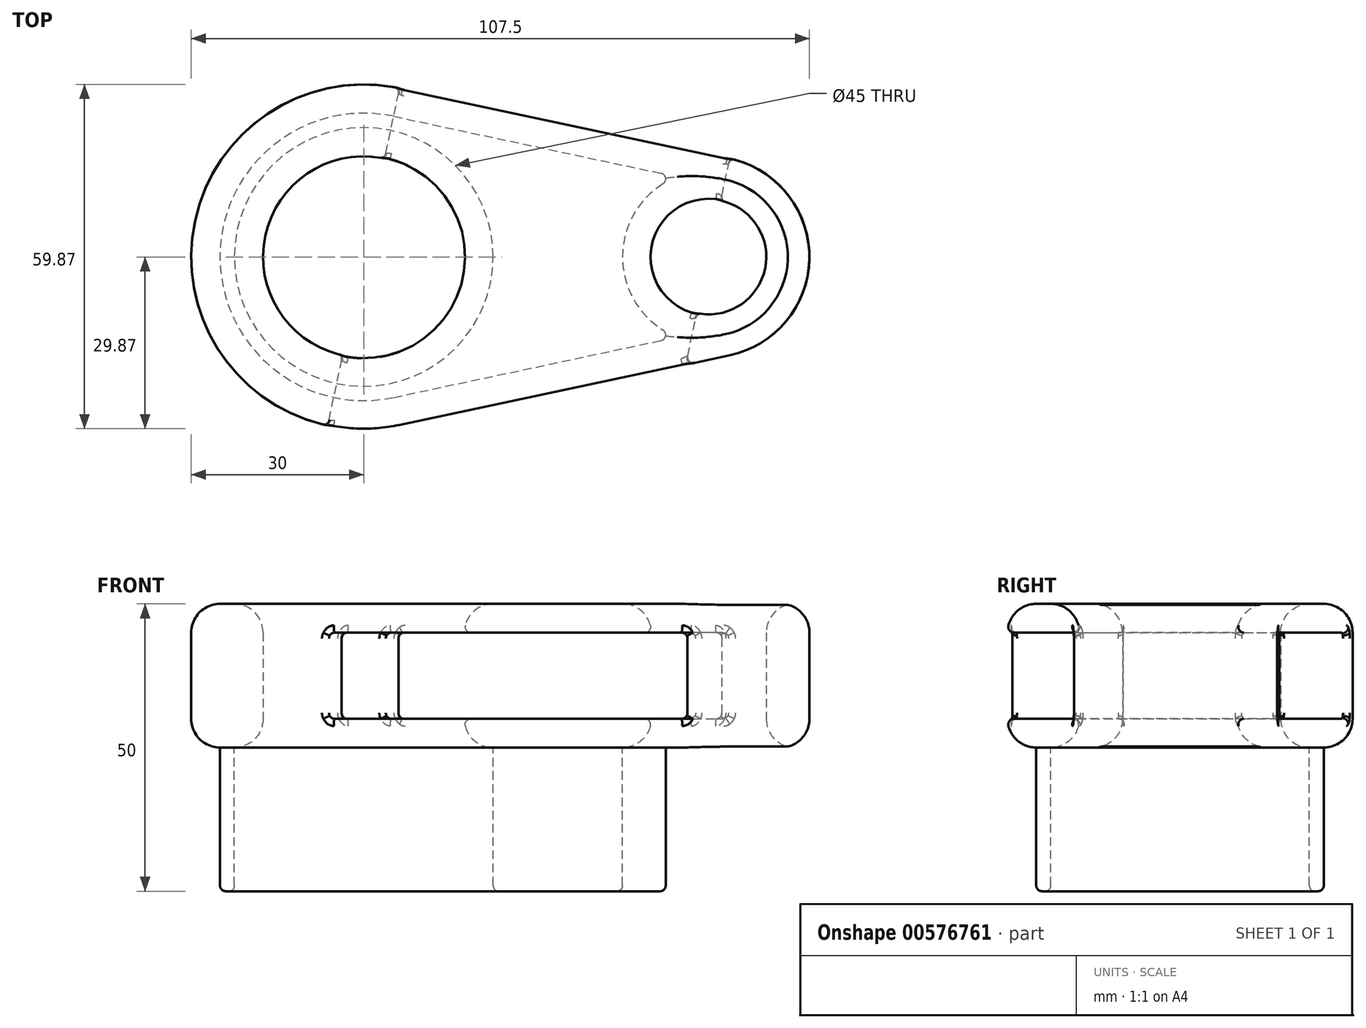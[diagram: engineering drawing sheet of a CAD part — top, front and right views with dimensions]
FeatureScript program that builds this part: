
annotation { "Feature Type Name" : "Feature", "Feature Type Description" : "" }
export const myFeature = defineFeature(function(context is Context, id is Id, definition is map)
    precondition{}
    {
        {
            var Q0;
            Q0=qCreatedBy(makeId("Top.planeOp"),FACE);
            var sketch = newSketch(context, id + "F0", { "sketchPlane" : qUnion([Q0])});
            skCircle(sketch, "E0", {"center": v(0, 0) * mm, "radius": 30 * mm});
            skCircle(sketch, "E1", {"center": v(60, 0) * mm, "radius": 17.5 * mm});
            skLineSegment(sketch, "E2", {"start": v(6.25, 29.34) * mm, "end": v(63.65, 17.12) * mm});
            skLineSegment(sketch, "E3", {"start": v(6.25, -29.34) * mm, "end": v(63.65, -17.12) * mm});
            skCircle(sketch, "E4", {"center": v(0, 0) * mm, "radius": 17.5 * mm});
            skCircle(sketch, "E5", {"center": v(60, 0) * mm, "radius": 10 * mm});
            skSolve(sketch);
        }
        {
            var Q0;
            {var subQ0=sQuery(id+"F0.wireOp",EDGE,"E2");Q0=makeQuery(id+"F0.imprint","IMPRINT",FACE,{"disambiguationData":[TD([[makeQuery(id+"F0.imprint","IMPRINT",EDGE,{"derivedFrom":subQ0}),-1.0]])]});}
            var Q1;
            Q1=makeQuery(id+"F0.imprint","IMPRINT",FACE,{"disambiguationData":[TD([[makeQuery(id+"F0.imprint","IMPRINT",EDGE,{"derivedFrom":sQuery(id+"F0.wireOp",EDGE,"E4")}),-1.0]])]});
            var Q2;
            Q2=makeQuery(id+"F0.imprint","IMPRINT",FACE,{"disambiguationData":[TD([[makeQuery(id+"F0.imprint","IMPRINT",EDGE,{"derivedFrom":sQuery(id+"F0.wireOp",EDGE,"E5")}),-1.0]])]});
            extrude(context, id + "F1", {"entities" : qUnion([Q0, Q1, Q2]), "depth" : 25 * mm, "offsetDistance" : 25 * mm});
        }
        {
            var Q0;
            Q0=makeQuery(id+"F1.opExtrude","CAP_EDGE",EDGE,{"disambiguationData":[OSD([sQuery(id+"F0.wireOp",EDGE,"E4")])],"isStart":false});
            var Q1;
            Q1=makeQuery(id+"F1.opExtrude","CAP_EDGE",EDGE,{"disambiguationData":[OSD([sQuery(id+"F0.wireOp",EDGE,"E2")])],"isStart":false});
            var Q2;
            Q2=makeQuery(id+"F1.opExtrude","CAP_EDGE",EDGE,{"disambiguationData":[OSD([sQuery(id+"F0.wireOp",EDGE,"E5")])],"isStart":false});
            var Q3;
            Q3=makeQuery(id+"F1.opExtrude","CAP_EDGE",EDGE,{"disambiguationData":[OSD([sQuery(id+"F0.wireOp",EDGE,"E4")])],"isStart":true});
            var Q4;
            Q4=makeQuery(id+"F1.opExtrude","CAP_EDGE",EDGE,{"disambiguationData":[OSD([sQuery(id+"F0.wireOp",EDGE,"E0")])],"isStart":true});
            var Q5;
            Q5=makeQuery(id+"F1.opExtrude","CAP_EDGE",EDGE,{"disambiguationData":[OSD([sQuery(id+"F0.wireOp",EDGE,"E5")])],"isStart":true});
            fillet(context, id + "F2", {"entities" : qUnion([Q0, Q1, Q2, Q3, Q4, Q5]), "radius" : 5 * mm, "tangentPropagation" : true, "allowEdgeOverflow" : false});
        }
        {
            var Q0;
            Q0=makeQuery(id+"F1.opExtrude","SWEPT_FACE",FACE,{"disambiguationData":[OSD([sQuery(id+"F0.wireOp",EDGE,"E2")])]});
            extrude(context, id + "F3", {"entities" : qUnion([Q0]), "operationType" : NewBodyOperationType.REMOVE, "endBound" : BoundingType.THROUGH_ALL, "oppositeDirection" : true, "depth" : 25 * mm, "offsetDistance" : 25 * mm});
        }
        {
            var Q0;
            {var subQ0=sQuery(id+"F0.wireOp",EDGE,"E2");var subQ1=sQuery(id+"F0.wireOp",EDGE,"E1");Q0=makeQuery(id+"F3.boolean.opBoolean","MERGE",EDGE,{"derivedFrom":[makeQuery(id+"F1.opExtrude","SWEPT_EDGE",EDGE,{"disambiguationData":[OSD([subQ1,subQ0])]}),makeQuery(id+"F3.opExtrude","CAP_EDGE",EDGE,{"disambiguationData":[OSD([subQ1,subQ0])],"isStart":true})]});}
            var Q1;
            {var subQ0=sQuery(id+"F0.wireOp",EDGE,"E2");var subQ1=makeQuery(id+"F2.opFillet","BLEND_EDGE",EDGE,{"blendedFrom":[makeQuery(id+"F1.opExtrude","CAP_EDGE",EDGE,{"disambiguationData":[OSD([subQ0])],"isStart":true}),makeQuery(id+"F1.opExtrude","SWEPT_FACE",FACE,{"disambiguationData":[OSD([subQ0])]})],"blendedInto":[makeQuery(id+"F1.opExtrude","SWEPT_FACE",FACE,{"disambiguationData":[OSD([subQ0])]})]});Q1=makeQuery(id+"F3.boolean.opBoolean","MERGE",EDGE,{"derivedFrom":[subQ1,makeQuery(id+"F3.opExtrude","CAP_EDGE",EDGE,{"disambiguationData":[OSD([subQ0]),TDD([subQ1])],"isStart":true})]});}
            var Q2;
            {var subQ0=sQuery(id+"F0.wireOp",EDGE,"E2");var subQ1=sQuery(id+"F0.wireOp",EDGE,"E0");Q2=makeQuery(id+"F3.boolean.opBoolean","MERGE",EDGE,{"derivedFrom":[makeQuery(id+"F1.opExtrude","SWEPT_EDGE",EDGE,{"disambiguationData":[OSD([subQ1,subQ0])]}),makeQuery(id+"F3.opExtrude","CAP_EDGE",EDGE,{"disambiguationData":[OSD([subQ1,subQ0])],"isStart":true})]});}
            var Q3;
            {var subQ0=sQuery(id+"F0.wireOp",EDGE,"E2");var subQ1=makeQuery(id+"F2.opFillet","BLEND_EDGE",EDGE,{"blendedFrom":[makeQuery(id+"F1.opExtrude","CAP_EDGE",EDGE,{"disambiguationData":[OSD([subQ0])],"isStart":false}),makeQuery(id+"F1.opExtrude","SWEPT_FACE",FACE,{"disambiguationData":[OSD([subQ0])]})],"blendedInto":[makeQuery(id+"F1.opExtrude","SWEPT_FACE",FACE,{"disambiguationData":[OSD([subQ0])]})]});Q3=makeQuery(id+"F3.boolean.opBoolean","MERGE",EDGE,{"derivedFrom":[subQ1,makeQuery(id+"F3.opExtrude","CAP_EDGE",EDGE,{"disambiguationData":[OSD([subQ0]),TDD([subQ1])],"isStart":true})]});}
            var Q4;
            {var subQ0=sQuery(id+"F0.wireOp",EDGE,"E0");var subQ1=makeQuery(id+"F1.opExtrude","CAP_EDGE",EDGE,{"disambiguationData":[OSD([subQ0])],"isStart":true});var subQ2=sQuery(id+"F0.wireOp",EDGE,"E4");var subQ3=sQuery(id+"F0.wireOp",EDGE,"E2");var subQ4=makeQuery(id+"F1.opExtrude","CAP_EDGE",EDGE,{"disambiguationData":[OSD([subQ3])],"isStart":true});var subQ5=makeQuery(id+"F1.opExtrude","SWEPT_FACE",FACE,{"disambiguationData":[OSD([subQ0])]});var subQ6=makeQuery(id+"F1.opExtrude","SWEPT_FACE",FACE,{"disambiguationData":[OSD([subQ3])]});Q4=makeQuery(id+"F3.boolean.opBoolean","COPY",EDGE,{"disambiguationData":[TD([subQ5,makeQuery(id+"F1.opExtrude","SWEPT_FACE",FACE,{"disambiguationData":[OSD([subQ2])]}),makeQuery(id+"F2.opFillet","BLEND_FACE",FACE,{"disambiguationData":[OSD([subQ0]),TDD([subQ1])]}),makeQuery(id+"F2.opFillet","BLEND_FACE",FACE,{"disambiguationData":[OSD([subQ3]),TDD([subQ4])]}),makeQuery(id+"F2.opFillet","BLEND_FACE",FACE,{"disambiguationData":[OSD([subQ2]),TDD([makeQuery(id+"F1.opExtrude","CAP_EDGE",EDGE,{"disambiguationData":[OSD([subQ2])],"isStart":true})])]}),makeQuery(id+"F3.opExtrude","SWEPT_FACE",FACE,{"disambiguationData":[OSD([subQ0,subQ3])]}),makeQuery(id+"F3.opExtrude","SWEPT_FACE",FACE,{"disambiguationData":[OSD([subQ3]),TDD([makeQuery(id+"F2.opFillet","BLEND_EDGE",EDGE,{"blendedFrom":[subQ4,subQ6],"blendedInto":[subQ6]})])]})])],"derivedFrom":makeQuery(id+"F3.opExtrude","SWEPT_EDGE",EDGE,{"disambiguationData":[OSD([subQ0,subQ3]),TDD([makeQuery(id+"F2.opFillet","BLEND_VERTEX",VERTEX,{"blendedFrom":[subQ1,subQ4,subQ5,subQ6],"blendedInto":[subQ5,subQ6]})])]})});}
            var Q5;
            {var subQ0=sQuery(id+"F0.wireOp",EDGE,"E0");var subQ1=makeQuery(id+"F1.opExtrude","CAP_EDGE",EDGE,{"disambiguationData":[OSD([subQ0])],"isStart":false});var subQ2=sQuery(id+"F0.wireOp",EDGE,"E2");var subQ3=makeQuery(id+"F1.opExtrude","CAP_EDGE",EDGE,{"disambiguationData":[OSD([subQ2])],"isStart":false});var subQ4=sQuery(id+"F0.wireOp",EDGE,"E4");var subQ5=makeQuery(id+"F1.opExtrude","SWEPT_FACE",FACE,{"disambiguationData":[OSD([subQ0])]});var subQ6=makeQuery(id+"F1.opExtrude","SWEPT_FACE",FACE,{"disambiguationData":[OSD([subQ2])]});Q5=makeQuery(id+"F3.boolean.opBoolean","COPY",EDGE,{"disambiguationData":[TD([subQ5,makeQuery(id+"F1.opExtrude","SWEPT_FACE",FACE,{"disambiguationData":[OSD([subQ4])]}),makeQuery(id+"F2.opFillet","BLEND_FACE",FACE,{"disambiguationData":[OSD([subQ0]),TDD([subQ1])]}),makeQuery(id+"F2.opFillet","BLEND_FACE",FACE,{"disambiguationData":[OSD([subQ2]),TDD([subQ3])]}),makeQuery(id+"F2.opFillet","BLEND_FACE",FACE,{"disambiguationData":[OSD([subQ4]),TDD([makeQuery(id+"F1.opExtrude","CAP_EDGE",EDGE,{"disambiguationData":[OSD([subQ4])],"isStart":false})])]}),makeQuery(id+"F3.opExtrude","SWEPT_FACE",FACE,{"disambiguationData":[OSD([subQ0,subQ2])]}),makeQuery(id+"F3.opExtrude","SWEPT_FACE",FACE,{"disambiguationData":[OSD([subQ2]),TDD([makeQuery(id+"F2.opFillet","BLEND_EDGE",EDGE,{"blendedFrom":[subQ3,subQ6],"blendedInto":[subQ6]})])]})])],"derivedFrom":makeQuery(id+"F3.opExtrude","SWEPT_EDGE",EDGE,{"disambiguationData":[OSD([subQ0,subQ2]),TDD([makeQuery(id+"F2.opFillet","BLEND_VERTEX",VERTEX,{"blendedFrom":[subQ1,subQ3,subQ5,subQ6],"blendedInto":[subQ5,subQ6]})])]})});}
            var Q6;
            {var subQ0=sQuery(id+"F0.wireOp",EDGE,"E2");var subQ1=makeQuery(id+"F1.opExtrude","CAP_EDGE",EDGE,{"disambiguationData":[OSD([subQ0])],"isStart":false});var subQ2=sQuery(id+"F0.wireOp",EDGE,"E1");var subQ3=makeQuery(id+"F1.opExtrude","CAP_EDGE",EDGE,{"disambiguationData":[OSD([subQ2])],"isStart":false});var subQ5=makeQuery(id+"F1.opExtrude","SWEPT_FACE",FACE,{"disambiguationData":[OSD([subQ2])]});var subQ6=makeQuery(id+"F1.opExtrude","SWEPT_FACE",FACE,{"disambiguationData":[OSD([subQ0])]});Q6=makeQuery(id+"F3.boolean.opBoolean","COPY",EDGE,{"disambiguationData":[TD([subQ5])],"derivedFrom":makeQuery(id+"F3.opExtrude","SWEPT_EDGE",EDGE,{"disambiguationData":[OSD([subQ2,subQ0]),TDD([makeQuery(id+"F2.opFillet","BLEND_VERTEX",VERTEX,{"blendedFrom":[subQ3,subQ1,subQ5,subQ6],"blendedInto":[subQ5,subQ6]})])]})});}
            var Q7;
            {var subQ0=sQuery(id+"F0.wireOp",EDGE,"E2");var subQ1=makeQuery(id+"F1.opExtrude","CAP_EDGE",EDGE,{"disambiguationData":[OSD([subQ0])],"isStart":true});var subQ3=sQuery(id+"F0.wireOp",EDGE,"E1");var subQ4=makeQuery(id+"F1.opExtrude","CAP_EDGE",EDGE,{"disambiguationData":[OSD([subQ3])],"isStart":true});var subQ5=makeQuery(id+"F1.opExtrude","SWEPT_FACE",FACE,{"disambiguationData":[OSD([subQ3])]});var subQ6=makeQuery(id+"F1.opExtrude","SWEPT_FACE",FACE,{"disambiguationData":[OSD([subQ0])]});Q7=makeQuery(id+"F3.boolean.opBoolean","COPY",EDGE,{"disambiguationData":[TD([subQ5])],"derivedFrom":makeQuery(id+"F3.opExtrude","SWEPT_EDGE",EDGE,{"disambiguationData":[OSD([subQ3,subQ0]),TDD([makeQuery(id+"F2.opFillet","BLEND_VERTEX",VERTEX,{"blendedFrom":[subQ4,subQ1,subQ5,subQ6],"blendedInto":[subQ5,subQ6]})])]})});}
            var Q8;
            {var subQ0=sQuery(id+"F0.wireOp",EDGE,"E5");var subQ1=makeQuery(id+"F1.opExtrude","CAP_EDGE",EDGE,{"disambiguationData":[OSD([subQ0])],"isStart":false});var subQ2=sQuery(id+"F0.wireOp",EDGE,"E2");Q8=makeQuery(id+"F3.boolean.opBoolean","SPLIT",EDGE,{"disambiguationData":[topologyDisambiguationEdgeConnected([makeQuery(id+"F3.opExtrude","SWEPT_FACE",FACE,{"disambiguationData":[OSD([subQ2]),TDD([makeQuery(id+"F2.opFillet","BLEND_EDGE",EDGE,{"blendedFrom":[makeQuery(id+"F1.opExtrude","CAP_EDGE",EDGE,{"disambiguationData":[OSD([subQ2])],"isStart":false}),makeQuery(id+"F1.opExtrude","SWEPT_FACE",FACE,{"disambiguationData":[OSD([subQ2])]})],"blendedInto":[makeQuery(id+"F1.opExtrude","SWEPT_FACE",FACE,{"disambiguationData":[OSD([subQ2])]})]})])]})])],"derivedFrom":makeQuery(id+"F2.opFillet","BLEND_EDGE",EDGE,{"blendedFrom":[subQ1,makeQuery(id+"F1.opExtrude","SWEPT_FACE",FACE,{"disambiguationData":[OSD([subQ0])]})],"blendedInto":[makeQuery(id+"F1.opExtrude","SWEPT_FACE",FACE,{"disambiguationData":[OSD([subQ0])]})]})});}
            var Q9;
            Q9=makeQuery(id+"F3.boolean.opBoolean","INTERSECT",EDGE,{"disambiguationData":[OD(0.0)],"derivedFrom":[makeQuery(id+"F1.opExtrude","SWEPT_FACE",FACE,{"disambiguationData":[OSD([sQuery(id+"F0.wireOp",EDGE,"E5")])]}),makeQuery(id+"F3.opExtrude","SWEPT_FACE",FACE,{"disambiguationData":[OSD([sQuery(id+"F0.wireOp",EDGE,"E1"),sQuery(id+"F0.wireOp",EDGE,"E2")])]})]});
            var Q10;
            {var subQ0=sQuery(id+"F0.wireOp",EDGE,"E5");var subQ1=makeQuery(id+"F1.opExtrude","CAP_EDGE",EDGE,{"disambiguationData":[OSD([subQ0])],"isStart":true});var subQ2=sQuery(id+"F0.wireOp",EDGE,"E2");Q10=makeQuery(id+"F3.boolean.opBoolean","SPLIT",EDGE,{"disambiguationData":[topologyDisambiguationEdgeConnected([makeQuery(id+"F3.opExtrude","SWEPT_FACE",FACE,{"disambiguationData":[OSD([subQ2]),TDD([makeQuery(id+"F2.opFillet","BLEND_EDGE",EDGE,{"blendedFrom":[makeQuery(id+"F1.opExtrude","CAP_EDGE",EDGE,{"disambiguationData":[OSD([subQ2])],"isStart":true}),makeQuery(id+"F1.opExtrude","SWEPT_FACE",FACE,{"disambiguationData":[OSD([subQ2])]})],"blendedInto":[makeQuery(id+"F1.opExtrude","SWEPT_FACE",FACE,{"disambiguationData":[OSD([subQ2])]})]})])]})])],"derivedFrom":makeQuery(id+"F2.opFillet","BLEND_EDGE",EDGE,{"blendedFrom":[subQ1,makeQuery(id+"F1.opExtrude","SWEPT_FACE",FACE,{"disambiguationData":[OSD([subQ0])]})],"blendedInto":[makeQuery(id+"F1.opExtrude","SWEPT_FACE",FACE,{"disambiguationData":[OSD([subQ0])]})]})});}
            var Q11;
            Q11=makeQuery(id+"F3.boolean.opBoolean","INTERSECT",EDGE,{"disambiguationData":[OD(1.0)],"derivedFrom":[makeQuery(id+"F1.opExtrude","SWEPT_FACE",FACE,{"disambiguationData":[OSD([sQuery(id+"F0.wireOp",EDGE,"E5")])]}),makeQuery(id+"F3.opExtrude","SWEPT_FACE",FACE,{"disambiguationData":[OSD([sQuery(id+"F0.wireOp",EDGE,"E1"),sQuery(id+"F0.wireOp",EDGE,"E2")])]})]});
            var Q12;
            Q12=makeQuery(id+"F3.boolean.opBoolean","INTERSECT",EDGE,{"disambiguationData":[OD(0.0)],"derivedFrom":[makeQuery(id+"F1.opExtrude","SWEPT_FACE",FACE,{"disambiguationData":[OSD([sQuery(id+"F0.wireOp",EDGE,"E4")])]}),makeQuery(id+"F3.opExtrude","SWEPT_FACE",FACE,{"disambiguationData":[OSD([sQuery(id+"F0.wireOp",EDGE,"E0"),sQuery(id+"F0.wireOp",EDGE,"E2")])]})]});
            var Q13;
            {var subQ0=sQuery(id+"F0.wireOp",EDGE,"E4");var subQ1=makeQuery(id+"F1.opExtrude","CAP_EDGE",EDGE,{"disambiguationData":[OSD([subQ0])],"isStart":true});var subQ2=sQuery(id+"F0.wireOp",EDGE,"E2");Q13=makeQuery(id+"F3.boolean.opBoolean","SPLIT",EDGE,{"disambiguationData":[topologyDisambiguationEdgeConnected([makeQuery(id+"F3.opExtrude","SWEPT_FACE",FACE,{"disambiguationData":[OSD([subQ2]),TDD([makeQuery(id+"F2.opFillet","BLEND_EDGE",EDGE,{"blendedFrom":[makeQuery(id+"F1.opExtrude","CAP_EDGE",EDGE,{"disambiguationData":[OSD([subQ2])],"isStart":true}),makeQuery(id+"F1.opExtrude","SWEPT_FACE",FACE,{"disambiguationData":[OSD([subQ2])]})],"blendedInto":[makeQuery(id+"F1.opExtrude","SWEPT_FACE",FACE,{"disambiguationData":[OSD([subQ2])]})]})])]})])],"derivedFrom":makeQuery(id+"F2.opFillet","BLEND_EDGE",EDGE,{"blendedFrom":[subQ1,makeQuery(id+"F1.opExtrude","SWEPT_FACE",FACE,{"disambiguationData":[OSD([subQ0])]})],"blendedInto":[makeQuery(id+"F1.opExtrude","SWEPT_FACE",FACE,{"disambiguationData":[OSD([subQ0])]})]})});}
            var Q14;
            Q14=makeQuery(id+"F3.boolean.opBoolean","INTERSECT",EDGE,{"disambiguationData":[OD(1.0)],"derivedFrom":[makeQuery(id+"F1.opExtrude","SWEPT_FACE",FACE,{"disambiguationData":[OSD([sQuery(id+"F0.wireOp",EDGE,"E4")])]}),makeQuery(id+"F3.opExtrude","SWEPT_FACE",FACE,{"disambiguationData":[OSD([sQuery(id+"F0.wireOp",EDGE,"E0"),sQuery(id+"F0.wireOp",EDGE,"E2")])]})]});
            var Q15;
            {var subQ0=sQuery(id+"F0.wireOp",EDGE,"E4");var subQ1=makeQuery(id+"F1.opExtrude","CAP_EDGE",EDGE,{"disambiguationData":[OSD([subQ0])],"isStart":false});var subQ2=sQuery(id+"F0.wireOp",EDGE,"E2");Q15=makeQuery(id+"F3.boolean.opBoolean","SPLIT",EDGE,{"disambiguationData":[topologyDisambiguationEdgeConnected([makeQuery(id+"F3.opExtrude","SWEPT_FACE",FACE,{"disambiguationData":[OSD([subQ2]),TDD([makeQuery(id+"F2.opFillet","BLEND_EDGE",EDGE,{"blendedFrom":[makeQuery(id+"F1.opExtrude","CAP_EDGE",EDGE,{"disambiguationData":[OSD([subQ2])],"isStart":false}),makeQuery(id+"F1.opExtrude","SWEPT_FACE",FACE,{"disambiguationData":[OSD([subQ2])]})],"blendedInto":[makeQuery(id+"F1.opExtrude","SWEPT_FACE",FACE,{"disambiguationData":[OSD([subQ2])]})]})])]})])],"derivedFrom":makeQuery(id+"F2.opFillet","BLEND_EDGE",EDGE,{"blendedFrom":[subQ1,makeQuery(id+"F1.opExtrude","SWEPT_FACE",FACE,{"disambiguationData":[OSD([subQ0])]})],"blendedInto":[makeQuery(id+"F1.opExtrude","SWEPT_FACE",FACE,{"disambiguationData":[OSD([subQ0])]})]})});}
            var Q16;
            {var subQ0=sQuery(id+"F0.wireOp",EDGE,"E3");var subQ1=makeQuery(id+"F1.opExtrude","CAP_EDGE",EDGE,{"disambiguationData":[OSD([subQ0])],"isStart":false});var subQ2=sQuery(id+"F0.wireOp",EDGE,"E2");Q16=makeQuery(id+"F3.boolean.opBoolean","SPLIT",EDGE,{"disambiguationData":[topologyDisambiguationEdgeConnected([makeQuery(id+"F3.opExtrude","SWEPT_FACE",FACE,{"disambiguationData":[OSD([subQ2]),TDD([makeQuery(id+"F2.opFillet","BLEND_EDGE",EDGE,{"blendedFrom":[makeQuery(id+"F1.opExtrude","CAP_EDGE",EDGE,{"disambiguationData":[OSD([subQ2])],"isStart":false}),makeQuery(id+"F1.opExtrude","SWEPT_FACE",FACE,{"disambiguationData":[OSD([subQ2])]})],"blendedInto":[makeQuery(id+"F1.opExtrude","SWEPT_FACE",FACE,{"disambiguationData":[OSD([subQ2])]})]})])]})])],"derivedFrom":makeQuery(id+"F2.opFillet","BLEND_EDGE",EDGE,{"blendedFrom":[subQ1,makeQuery(id+"F1.opExtrude","SWEPT_FACE",FACE,{"disambiguationData":[OSD([subQ0])]})],"blendedInto":[makeQuery(id+"F1.opExtrude","SWEPT_FACE",FACE,{"disambiguationData":[OSD([subQ0])]})]})});}
            var Q17;
            {var subQ0=sQuery(id+"F0.wireOp",EDGE,"E0");var subQ1=makeQuery(id+"F1.opExtrude","CAP_EDGE",EDGE,{"disambiguationData":[OSD([subQ0])],"isStart":false});var subQ2=sQuery(id+"F0.wireOp",EDGE,"E2");Q17=makeQuery(id+"F3.boolean.opBoolean","SPLIT",EDGE,{"disambiguationData":[topologyDisambiguationEdgeConnected([makeQuery(id+"F3.opExtrude","SWEPT_FACE",FACE,{"disambiguationData":[OSD([subQ2]),TDD([makeQuery(id+"F2.opFillet","BLEND_EDGE",EDGE,{"blendedFrom":[makeQuery(id+"F1.opExtrude","CAP_EDGE",EDGE,{"disambiguationData":[OSD([subQ2])],"isStart":false}),makeQuery(id+"F1.opExtrude","SWEPT_FACE",FACE,{"disambiguationData":[OSD([subQ2])]})],"blendedInto":[makeQuery(id+"F1.opExtrude","SWEPT_FACE",FACE,{"disambiguationData":[OSD([subQ2])]})]})])]})])],"derivedFrom":makeQuery(id+"F2.opFillet","BLEND_EDGE",EDGE,{"blendedFrom":[subQ1,makeQuery(id+"F1.opExtrude","SWEPT_FACE",FACE,{"disambiguationData":[OSD([subQ0])]})],"blendedInto":[makeQuery(id+"F1.opExtrude","SWEPT_FACE",FACE,{"disambiguationData":[OSD([subQ0])]})]})});}
            var Q18;
            {var subQ0=sQuery(id+"F0.wireOp",EDGE,"E0");Q18=makeQuery(id+"F3.boolean.opBoolean","INTERSECT",EDGE,{"derivedFrom":[makeQuery(id+"F1.opExtrude","SWEPT_FACE",FACE,{"disambiguationData":[OSD([subQ0])]}),makeQuery(id+"F3.opExtrude","SWEPT_FACE",FACE,{"disambiguationData":[OSD([subQ0,sQuery(id+"F0.wireOp",EDGE,"E2")])]})]});}
            var Q19;
            {var subQ0=sQuery(id+"F0.wireOp",EDGE,"E0");var subQ1=makeQuery(id+"F1.opExtrude","CAP_EDGE",EDGE,{"disambiguationData":[OSD([subQ0])],"isStart":false});var subQ2=sQuery(id+"F0.wireOp",EDGE,"E4");var subQ3=makeQuery(id+"F1.opExtrude","SWEPT_FACE",FACE,{"disambiguationData":[OSD([subQ0])]});var subQ4=sQuery(id+"F0.wireOp",EDGE,"E2");var subQ5=makeQuery(id+"F1.opExtrude","SWEPT_FACE",FACE,{"disambiguationData":[OSD([subQ4])]});var subQ6=makeQuery(id+"F1.opExtrude","CAP_EDGE",EDGE,{"disambiguationData":[OSD([subQ4])],"isStart":false});Q19=makeQuery(id+"F3.boolean.opBoolean","COPY",EDGE,{"disambiguationData":[TD([subQ3,makeQuery(id+"F1.opExtrude","SWEPT_FACE",FACE,{"disambiguationData":[OSD([subQ2])]}),makeQuery(id+"F2.opFillet","BLEND_FACE",FACE,{"disambiguationData":[OSD([subQ0]),TDD([subQ1])]}),makeQuery(id+"F2.opFillet","BLEND_FACE",FACE,{"disambiguationData":[OSD([subQ2]),TDD([makeQuery(id+"F1.opExtrude","CAP_EDGE",EDGE,{"disambiguationData":[OSD([subQ2])],"isStart":false})])]}),makeQuery(id+"F3.opExtrude","SWEPT_FACE",FACE,{"disambiguationData":[OSD([subQ0,subQ4])]}),makeQuery(id+"F3.opExtrude","SWEPT_FACE",FACE,{"disambiguationData":[OSD([subQ4]),TDD([makeQuery(id+"F2.opFillet","BLEND_EDGE",EDGE,{"blendedFrom":[subQ6,subQ5],"blendedInto":[subQ5]})])]})])],"derivedFrom":makeQuery(id+"F3.opExtrude","SWEPT_EDGE",EDGE,{"disambiguationData":[OSD([subQ0,subQ4]),TDD([makeQuery(id+"F2.opFillet","BLEND_VERTEX",VERTEX,{"blendedFrom":[subQ1,subQ6,subQ3,subQ5],"blendedInto":[subQ3,subQ5]})])]})});}
            var Q20;
            {var subQ0=sQuery(id+"F0.wireOp",EDGE,"E0");var subQ1=makeQuery(id+"F1.opExtrude","CAP_EDGE",EDGE,{"disambiguationData":[OSD([subQ0])],"isStart":true});var subQ2=sQuery(id+"F0.wireOp",EDGE,"E2");Q20=makeQuery(id+"F3.boolean.opBoolean","SPLIT",EDGE,{"disambiguationData":[topologyDisambiguationEdgeConnected([makeQuery(id+"F3.opExtrude","SWEPT_FACE",FACE,{"disambiguationData":[OSD([subQ2]),TDD([makeQuery(id+"F2.opFillet","BLEND_EDGE",EDGE,{"blendedFrom":[makeQuery(id+"F1.opExtrude","CAP_EDGE",EDGE,{"disambiguationData":[OSD([subQ2])],"isStart":true}),makeQuery(id+"F1.opExtrude","SWEPT_FACE",FACE,{"disambiguationData":[OSD([subQ2])]})],"blendedInto":[makeQuery(id+"F1.opExtrude","SWEPT_FACE",FACE,{"disambiguationData":[OSD([subQ2])]})]})])]})])],"derivedFrom":makeQuery(id+"F2.opFillet","BLEND_EDGE",EDGE,{"blendedFrom":[subQ1,makeQuery(id+"F1.opExtrude","SWEPT_FACE",FACE,{"disambiguationData":[OSD([subQ0])]})],"blendedInto":[makeQuery(id+"F1.opExtrude","SWEPT_FACE",FACE,{"disambiguationData":[OSD([subQ0])]})]})});}
            var Q21;
            {var subQ0=sQuery(id+"F0.wireOp",EDGE,"E3");var subQ1=makeQuery(id+"F1.opExtrude","CAP_EDGE",EDGE,{"disambiguationData":[OSD([subQ0])],"isStart":true});var subQ2=sQuery(id+"F0.wireOp",EDGE,"E2");Q21=makeQuery(id+"F3.boolean.opBoolean","SPLIT",EDGE,{"disambiguationData":[topologyDisambiguationEdgeConnected([makeQuery(id+"F3.opExtrude","SWEPT_FACE",FACE,{"disambiguationData":[OSD([subQ2]),TDD([makeQuery(id+"F2.opFillet","BLEND_EDGE",EDGE,{"blendedFrom":[makeQuery(id+"F1.opExtrude","CAP_EDGE",EDGE,{"disambiguationData":[OSD([subQ2])],"isStart":true}),makeQuery(id+"F1.opExtrude","SWEPT_FACE",FACE,{"disambiguationData":[OSD([subQ2])]})],"blendedInto":[makeQuery(id+"F1.opExtrude","SWEPT_FACE",FACE,{"disambiguationData":[OSD([subQ2])]})]})])]})])],"derivedFrom":makeQuery(id+"F2.opFillet","BLEND_EDGE",EDGE,{"blendedFrom":[subQ1,makeQuery(id+"F1.opExtrude","SWEPT_FACE",FACE,{"disambiguationData":[OSD([subQ0])]})],"blendedInto":[makeQuery(id+"F1.opExtrude","SWEPT_FACE",FACE,{"disambiguationData":[OSD([subQ0])]})]})});}
            var Q22;
            Q22=makeQuery(id+"F3.boolean.opBoolean","INTERSECT",EDGE,{"derivedFrom":[makeQuery(id+"F1.opExtrude","SWEPT_FACE",FACE,{"disambiguationData":[OSD([sQuery(id+"F0.wireOp",EDGE,"E3")])]}),makeQuery(id+"F3.opExtrude","SWEPT_FACE",FACE,{"disambiguationData":[OSD([sQuery(id+"F0.wireOp",EDGE,"E1"),sQuery(id+"F0.wireOp",EDGE,"E2")])]})]});
            var Q23;
            {var subQ0=sQuery(id+"F0.wireOp",EDGE,"E4");var subQ1=sQuery(id+"F0.wireOp",EDGE,"E0");var subQ2=makeQuery(id+"F1.opExtrude","CAP_EDGE",EDGE,{"disambiguationData":[OSD([subQ1])],"isStart":true});var subQ3=makeQuery(id+"F1.opExtrude","SWEPT_FACE",FACE,{"disambiguationData":[OSD([subQ1])]});var subQ4=sQuery(id+"F0.wireOp",EDGE,"E2");var subQ5=makeQuery(id+"F1.opExtrude","SWEPT_FACE",FACE,{"disambiguationData":[OSD([subQ4])]});var subQ6=makeQuery(id+"F1.opExtrude","CAP_EDGE",EDGE,{"disambiguationData":[OSD([subQ4])],"isStart":true});Q23=makeQuery(id+"F3.boolean.opBoolean","COPY",EDGE,{"disambiguationData":[TD([subQ3,makeQuery(id+"F1.opExtrude","SWEPT_FACE",FACE,{"disambiguationData":[OSD([subQ0])]}),makeQuery(id+"F2.opFillet","BLEND_FACE",FACE,{"disambiguationData":[OSD([subQ1]),TDD([subQ2])]}),makeQuery(id+"F2.opFillet","BLEND_FACE",FACE,{"disambiguationData":[OSD([subQ0]),TDD([makeQuery(id+"F1.opExtrude","CAP_EDGE",EDGE,{"disambiguationData":[OSD([subQ0])],"isStart":true})])]}),makeQuery(id+"F3.opExtrude","SWEPT_FACE",FACE,{"disambiguationData":[OSD([subQ1,subQ4])]}),makeQuery(id+"F3.opExtrude","SWEPT_FACE",FACE,{"disambiguationData":[OSD([subQ4]),TDD([makeQuery(id+"F2.opFillet","BLEND_EDGE",EDGE,{"blendedFrom":[subQ6,subQ5],"blendedInto":[subQ5]})])]})])],"derivedFrom":makeQuery(id+"F3.opExtrude","SWEPT_EDGE",EDGE,{"disambiguationData":[OSD([subQ1,subQ4]),TDD([makeQuery(id+"F2.opFillet","BLEND_VERTEX",VERTEX,{"blendedFrom":[subQ2,subQ6,subQ3,subQ5],"blendedInto":[subQ3,subQ5]})])]})});}
            var Q24;
            {var subQ0=sQuery(id+"F0.wireOp",EDGE,"E3");var subQ1=sQuery(id+"F0.wireOp",EDGE,"E2");var subQ2=makeQuery(id+"F1.opExtrude","SWEPT_FACE",FACE,{"disambiguationData":[OSD([subQ1])]});var subQ3=makeQuery(id+"F1.opExtrude","CAP_EDGE",EDGE,{"disambiguationData":[OSD([subQ1])],"isStart":false});var subQ5=sQuery(id+"F0.wireOp",EDGE,"E1");Q24=makeQuery(id+"F3.boolean.opBoolean","COPY",EDGE,{"disambiguationData":[TD([makeQuery(id+"F1.opExtrude","SWEPT_FACE",FACE,{"disambiguationData":[OSD([subQ0])]})])],"derivedFrom":makeQuery(id+"F3.opExtrude","SWEPT_EDGE",EDGE,{"disambiguationData":[OSD([subQ5,subQ1]),TDD([makeQuery(id+"F2.opFillet","BLEND_VERTEX",VERTEX,{"blendedFrom":[makeQuery(id+"F1.opExtrude","CAP_EDGE",EDGE,{"disambiguationData":[OSD([subQ5])],"isStart":false}),subQ3,makeQuery(id+"F1.opExtrude","SWEPT_FACE",FACE,{"disambiguationData":[OSD([subQ5])]}),subQ2],"blendedInto":[makeQuery(id+"F1.opExtrude","SWEPT_FACE",FACE,{"disambiguationData":[OSD([subQ5])]}),subQ2]})])]})});}
            var Q25;
            {var subQ1=sQuery(id+"F0.wireOp",EDGE,"E3");var subQ2=sQuery(id+"F0.wireOp",EDGE,"E2");var subQ3=makeQuery(id+"F1.opExtrude","SWEPT_FACE",FACE,{"disambiguationData":[OSD([subQ2])]});var subQ4=makeQuery(id+"F1.opExtrude","CAP_EDGE",EDGE,{"disambiguationData":[OSD([subQ2])],"isStart":true});var subQ5=sQuery(id+"F0.wireOp",EDGE,"E1");Q25=makeQuery(id+"F3.boolean.opBoolean","COPY",EDGE,{"disambiguationData":[TD([makeQuery(id+"F1.opExtrude","SWEPT_FACE",FACE,{"disambiguationData":[OSD([subQ1])]})])],"derivedFrom":makeQuery(id+"F3.opExtrude","SWEPT_EDGE",EDGE,{"disambiguationData":[OSD([subQ5,subQ2]),TDD([makeQuery(id+"F2.opFillet","BLEND_VERTEX",VERTEX,{"blendedFrom":[makeQuery(id+"F1.opExtrude","CAP_EDGE",EDGE,{"disambiguationData":[OSD([subQ5])],"isStart":true}),subQ4,makeQuery(id+"F1.opExtrude","SWEPT_FACE",FACE,{"disambiguationData":[OSD([subQ5])]}),subQ3],"blendedInto":[makeQuery(id+"F1.opExtrude","SWEPT_FACE",FACE,{"disambiguationData":[OSD([subQ5])]}),subQ3]})])]})});}
            fillet(context, id + "F4", {"entities" : qUnion([Q0, Q1, Q2, Q3, Q4, Q5, Q6, Q7, Q8, Q9, Q10, Q11, Q12, Q13, Q14, Q15, Q16, Q17, Q18, Q19, Q20, Q21, Q22, Q23, Q24, Q25]), "radius" : 1 * mm, "tangentPropagation" : true, "allowEdgeOverflow" : false});
        }
        {
            var Q0;
            Q0=makeQuery(id+"F1.opExtrude","CAP_FACE",FACE,{"disambiguationData":[OSD([sQuery(id+"F0.wireOp",EDGE,"E0"),sQuery(id+"F0.wireOp",EDGE,"E1"),sQuery(id+"F0.wireOp",EDGE,"E2"),sQuery(id+"F0.wireOp",EDGE,"E3"),sQuery(id+"F0.wireOp",EDGE,"E4"),sQuery(id+"F0.wireOp",EDGE,"E5")])],"isStart":true});
            extrude(context, id + "F5", {"entities" : qUnion([Q0]), "operationType" : NewBodyOperationType.ADD, "depth" : 25 * mm, "offsetDistance" : 25 * mm});
        }
        {
            var Q0;
            Q0=makeQuery(id+"F5.opExtrude","CAP_FACE",FACE,{"disambiguationData":[OSD([sQuery(id+"F0.wireOp",EDGE,"E0"),sQuery(id+"F0.wireOp",EDGE,"E1"),sQuery(id+"F0.wireOp",EDGE,"E2"),sQuery(id+"F0.wireOp",EDGE,"E3"),sQuery(id+"F0.wireOp",EDGE,"E4"),sQuery(id+"F0.wireOp",EDGE,"E5")])],"isStart":false});
            var Q1;
            {var subQ0=sQuery(id+"F0.wireOp",EDGE,"E5");var subQ1=sQuery(id+"F0.wireOp",EDGE,"E4");var subQ2=sQuery(id+"F0.wireOp",EDGE,"E3");var subQ3=sQuery(id+"F0.wireOp",EDGE,"E2");var subQ4=sQuery(id+"F0.wireOp",EDGE,"E1");var subQ5=sQuery(id+"F0.wireOp",EDGE,"E0");Q1=makeQuery(id+"F5.opExtrude","SWEPT_EDGE",EDGE,{"disambiguationData":[OSD([subQ5,subQ4,subQ3,subQ2,subQ1,subQ0]),TDD([makeQuery(id+"F2.opFillet","BLEND_VERTEX",VERTEX,{"blendedFrom":[makeQuery(id+"F1.opExtrude","CAP_EDGE",EDGE,{"disambiguationData":[OSD([subQ2])],"isStart":true}),makeQuery(id+"F1.opExtrude","CAP_EDGE",EDGE,{"disambiguationData":[OSD([subQ0])],"isStart":true}),makeQuery(id+"F1.opExtrude","CAP_FACE",FACE,{"disambiguationData":[OSD([subQ5,subQ4,subQ3,subQ2,subQ1,subQ0])],"isStart":true})],"blendedInto":[makeQuery(id+"F1.opExtrude","CAP_FACE",FACE,{"disambiguationData":[OSD([subQ5,subQ4,subQ3,subQ2,subQ1,subQ0])],"isStart":true})]})])]});}
            var Q2;
            {var subQ0=sQuery(id+"F0.wireOp",EDGE,"E5");var subQ1=sQuery(id+"F0.wireOp",EDGE,"E4");var subQ2=sQuery(id+"F0.wireOp",EDGE,"E3");var subQ3=sQuery(id+"F0.wireOp",EDGE,"E2");var subQ4=sQuery(id+"F0.wireOp",EDGE,"E1");var subQ5=sQuery(id+"F0.wireOp",EDGE,"E0");Q2=makeQuery(id+"F5.opExtrude","SWEPT_EDGE",EDGE,{"disambiguationData":[OSD([subQ5,subQ4,subQ3,subQ2,subQ1,subQ0]),TDD([makeQuery(id+"F2.opFillet","BLEND_VERTEX",VERTEX,{"blendedFrom":[makeQuery(id+"F1.opExtrude","CAP_EDGE",EDGE,{"disambiguationData":[OSD([subQ3])],"isStart":true}),makeQuery(id+"F1.opExtrude","CAP_EDGE",EDGE,{"disambiguationData":[OSD([subQ0])],"isStart":true}),makeQuery(id+"F1.opExtrude","CAP_FACE",FACE,{"disambiguationData":[OSD([subQ5,subQ4,subQ3,subQ2,subQ1,subQ0])],"isStart":true})],"blendedInto":[makeQuery(id+"F1.opExtrude","CAP_FACE",FACE,{"disambiguationData":[OSD([subQ5,subQ4,subQ3,subQ2,subQ1,subQ0])],"isStart":true})]})])]});}
            fillet(context, id + "F6", {"entities" : qUnion([Q0, Q1, Q2]), "radius" : 1 * mm, "tangentPropagation" : true, "allowEdgeOverflow" : false});
        }
    });
